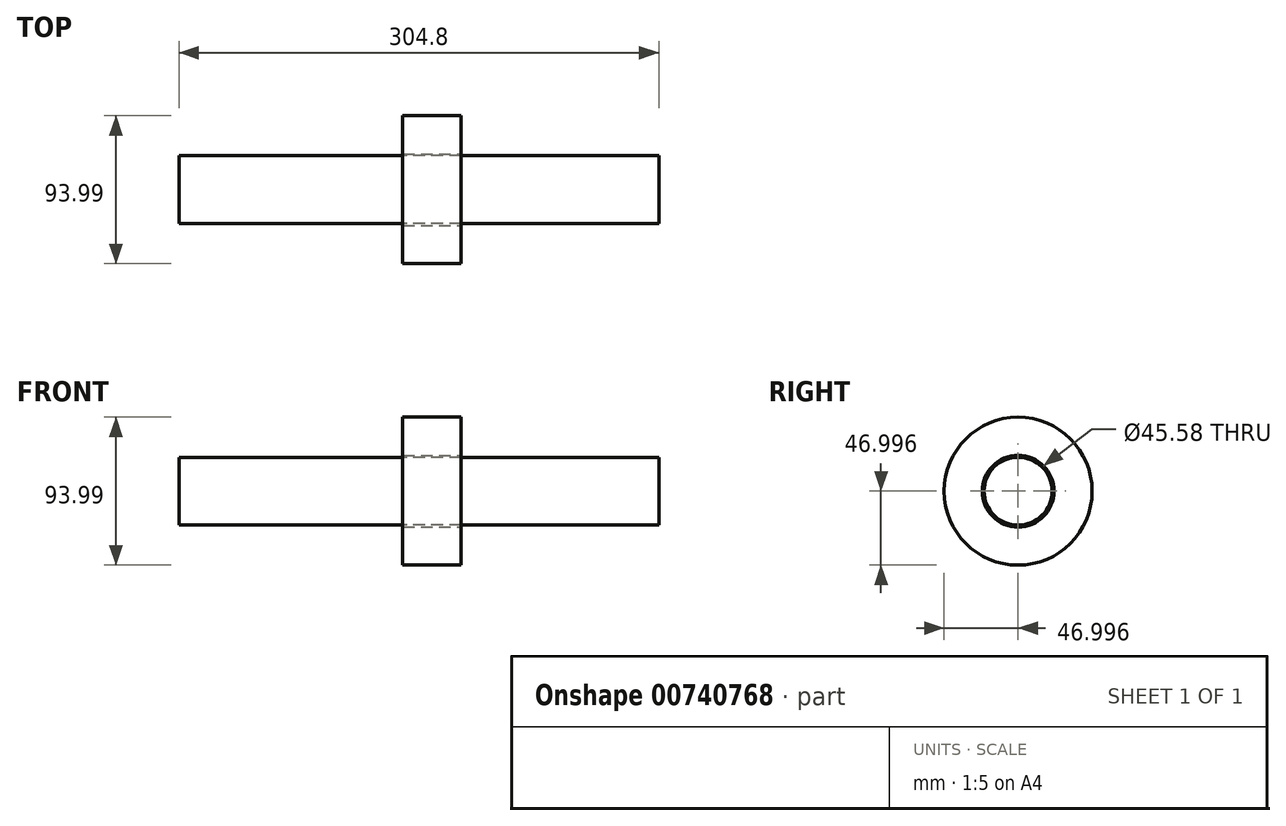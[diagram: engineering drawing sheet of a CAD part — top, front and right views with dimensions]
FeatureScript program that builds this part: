
annotation { "Feature Type Name" : "Feature", "Feature Type Description" : "" }
export const myFeature = defineFeature(function(context is Context, id is Id, definition is map)
    precondition{}
    {
        {
            var Q0;
            Q0=qCreatedBy(makeId("Right.planeOp"),FACE);
            var sketch = newSketch(context, id + "F0", { "sketchPlane" : qUnion([Q0])});
            skCircle(sketch, "E0", {"center": v(0.04, -0.76) * mm, "radius": 21.56 * mm});
            skSolve(sketch);
        }
        {
            var Q0;
            Q0 = qSketchRegion(id + "F0", true);
            extrude(context, id + "F1", {"entities" : qUnion([Q0]), "depth" : 304.8 * mm, "offsetDistance" : 25.4 * mm});
        }
        {
            var Q0;
            Q0=qCreatedBy(makeId("Front.planeOp"),FACE);
            var sketch = newSketch(context, id + "F2", { "sketchPlane" : qUnion([Q0])});
            skLineSegment(sketch, "E1.bottom", {"start": v(142.19, 46.23) * mm, "end": v(179.29, 46.23) * mm});
            skLineSegment(sketch, "E1.top", {"start": v(142.19, 22.03) * mm, "end": v(179.29, 22.03) * mm});
            skLineSegment(sketch, "E1.left", {"start": v(142.19, 46.23) * mm, "end": v(142.19, 22.03) * mm});
            skLineSegment(sketch, "E1.right", {"start": v(179.29, 46.23) * mm, "end": v(179.29, 22.03) * mm});
            skSolve(sketch);
        }
        {
            var Q0;
            Q0=makeQuery(id+"F2.imprint","IMPRINT",FACE,{"disambiguationData":[TD([[makeQuery(id+"F2.imprint","IMPRINT",EDGE,{"derivedFrom":sQuery(id+"F2.wireOp",EDGE,"E1.bottom")}),-1.0]])]});
            var Q1;
            Q1=makeQuery(id+"F1.opExtrude","SWEPT_FACE",FACE,{"disambiguationData":[OSD([sQuery(id+"F0.wireOp",EDGE,"E0")])]});
            revolve(context, id + "F3", {"surfaceOperationType" : NewSurfaceOperationType.NEW, "entities" : qUnion([Q0]), "axis" : qUnion([Q1]), "revolveType" : RevolveType.FULL});
        }
    });
